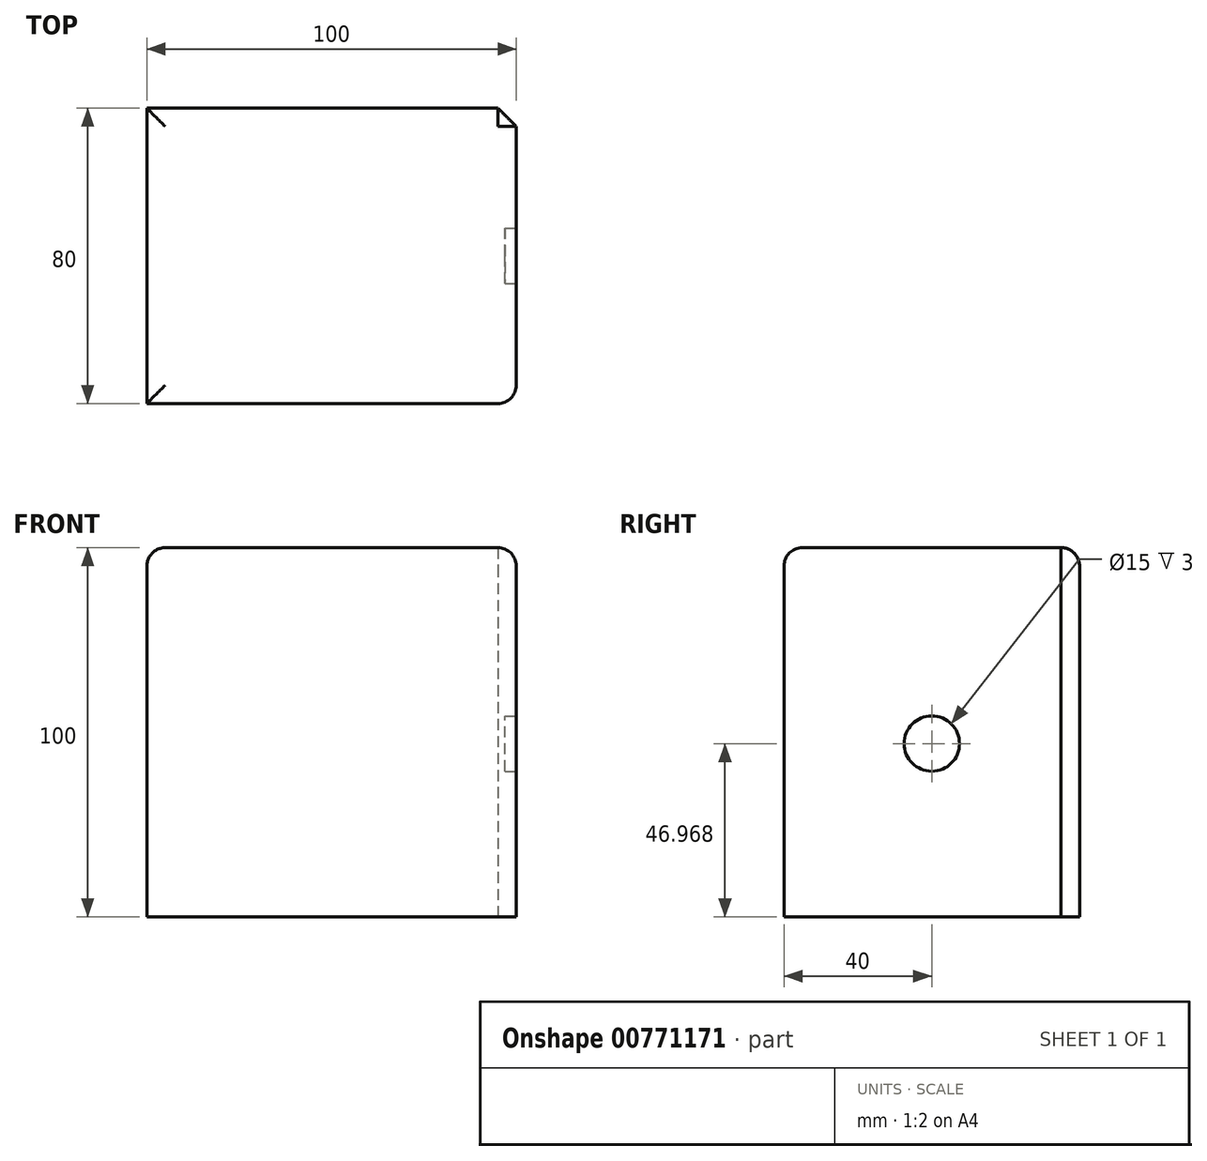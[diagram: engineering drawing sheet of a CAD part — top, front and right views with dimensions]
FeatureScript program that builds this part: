
annotation { "Feature Type Name" : "Feature", "Feature Type Description" : "" }
export const myFeature = defineFeature(function(context is Context, id is Id, definition is map)
    precondition{}
    {
        {
            var Q0;
            Q0=qCreatedBy(makeId("Top.planeOp"),FACE);
            var sketch = newSketch(context, id + "F0", { "sketchPlane" : qUnion([Q0])});
            skLineSegment(sketch, "E0.bottom", {"start": v(50, -40) * mm, "end": v(-50, -40) * mm});
            skLineSegment(sketch, "E0.top", {"start": v(50, 40) * mm, "end": v(-50, 40) * mm});
            skLineSegment(sketch, "E0.left", {"start": v(50, -40) * mm, "end": v(50, 40) * mm});
            skLineSegment(sketch, "E0.right", {"start": v(-50, -40) * mm, "end": v(-50, 40) * mm});
            skPoint(sketch, "E0.middle", {"position": v(0, 0) * mm});
            skSolve(sketch);
        }
        {
            var Q0;
            Q0=makeQuery(id+"F0.imprint","IMPRINT",FACE,{"disambiguationData":[TD([[makeQuery(id+"F0.imprint","IMPRINT",EDGE,{"derivedFrom":sQuery(id+"F0.wireOp",EDGE,"E0.bottom")}),-1.0]])]});
            extrude(context, id + "F1", {"entities" : qUnion([Q0]), "depth" : 100 * mm, "offsetDistance" : 25 * mm});
        }
        {
            var Q0;
            Q0=makeQuery(id+"F1.opExtrude","SWEPT_FACE",FACE,{"disambiguationData":[OSD([sQuery(id+"F0.wireOp",EDGE,"E0.left")])]});
            var sketch = newSketch(context, id + "F2", { "sketchPlane" : qUnion([Q0])});
            skCircle(sketch, "E1", {"center": v(0, 46.97) * mm, "radius": 7.5 * mm});
            skSolve(sketch);
        }
        {
            var Q0;
            Q0=makeQuery(id+"F2.imprint","IMPRINT",FACE,{"disambiguationData":[TD([[makeQuery(id+"F2.imprint","IMPRINT",EDGE,{"derivedFrom":sQuery(id+"F2.wireOp",EDGE,"E1")}),1.0]])]});
            var Q1;
            Q1=sQuery(id+"F2.wireOp",EDGE,"E1");
            extrude(context, id + "F3", {"entities" : qUnion([Q0]), "operationType" : NewBodyOperationType.REMOVE, "surfaceEntities" : qUnion([Q1]), "oppositeDirection" : true, "depth" : 3 * mm, "offsetDistance" : 25 * mm});
        }
        {
            var Q0;
            Q0=makeQuery(id+"F1.opExtrude","CAP_FACE",FACE,{"disambiguationData":[OSD([sQuery(id+"F0.wireOp",EDGE,"E0.bottom"),sQuery(id+"F0.wireOp",EDGE,"E0.top"),sQuery(id+"F0.wireOp",EDGE,"E0.left"),sQuery(id+"F0.wireOp",EDGE,"E0.right")])],"isStart":false});
            var Q1;
            Q1=makeQuery(id+"F1.opExtrude","SWEPT_EDGE",EDGE,{"disambiguationData":[OSD([sQuery(id+"F0.wireOp",EDGE,"E0.bottom"),sQuery(id+"F0.wireOp",EDGE,"E0.left")])]});
            fillet(context, id + "F4", {"entities" : qUnion([Q0, Q1]), "radius" : 5 * mm, "tangentPropagation" : true, "allowEdgeOverflow" : false});
        }
        {
            var Q0;
            Q0=makeQuery(id+"F1.opExtrude","SWEPT_EDGE",EDGE,{"disambiguationData":[OSD([sQuery(id+"F0.wireOp",EDGE,"E0.top"),sQuery(id+"F0.wireOp",EDGE,"E0.left")])]});
            chamfer(context, id + "F5", {"entities" : qUnion([Q0]), "width" : 5 * mm, "tangentPropagation" : true});
        }
    });
